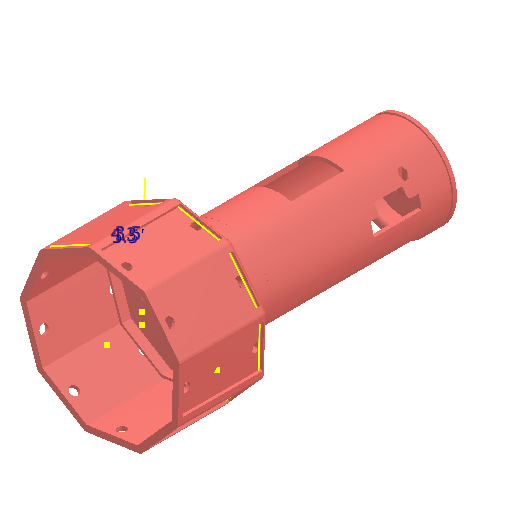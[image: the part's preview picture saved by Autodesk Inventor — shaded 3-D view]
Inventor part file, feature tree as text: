
AUTODESK INVENTOR PART (.ipt)
format: ipt  version: 2025 (Build 290162000, 162)  size: 1,940,480 bytes
history: native  units: in
note: dims shown in document units (in); Inventor stores cm internally (conversion verified against a paired STEP export)
features: sketch x63, extrude x58, fillet x11, plane x6, other x3, direct_edit x2, pattern_circular x2, move_body x2, reference x2, emboss x1, split x1, projected_geometry x1
ambient origin geometry x8: Origin, YZ Plane, XZ Plane, XY Plane, X Axis, Y Axis, Z Axis, Center Point
bodies: Solid1 (feature_tree), Body4 (feature_tree), Solid2 (feature_tree), Solid3 (feature_tree)
feature tree (152):
  direct_edit  "Direct Edit1"
  extrude  "Extrusion1"  Depth=0.2062in TaperAngle=0.0deg
  extrude  "Extrusion2"  Depth=0.1437in TaperAngle=0.0deg
  sketch  "Sketch3"  dims[d8=0.0787in d9=1.811in d10=0.0in]
  extrude  "Extrusion3"  Depth=1.811in TaperAngle=0.0deg
  sketch  "Sketch6"  dims[d13=0.0591in d14=0.0in d15=0.1969in]
  extrude  "Extrusion4"  Depth=0.9449in
  extrude  "Extrusion5"  Depth=0.1969in
  pattern_circular  "Circular Pattern1"  Count=9  [1 undecoded]
  extrude  "Extrusion6"  Depth=0.315in
  extrude  "Extrusion7"  Depth=1.4409in TaperAngle=0.0deg
  pattern_circular  "Circular Pattern2"  Count=9  [1 undecoded]
  fillet  "Fillet1"  Radius=0.1412in
  extrude  "Extrusion8"  Depth=0.063in
  extrude  "Extrusion9"  Depth=0.8312in TaperAngle=0.0deg
  extrude  "Extrusion10"  Depth=0.0787in
  extrude  "Extrusion11"  Depth=0.1688in TaperAngle=0.0deg
  direct_edit  "Direct Edit2"
  extrude  "Extrusion12"  Depth=1.1063in TaperAngle=0.0deg
  extrude  "Extrusion13"  Depth=0.4724in TaperAngle=0.0deg
  extrude  "Extrusion14"  Depth=1.8898in
  extrude  "Extrusion15"  Depth=1.2795in
  extrude  "Extrusion16"  Depth=0.0787in TaperAngle=0.0deg
  extrude  "Extrusion17"  Depth=0.0787in
  fillet  "Fillet2"  Radius=0.0787in
  fillet  "Fillet3"  Radius=0.0787in
  fillet  "Fillet4"  Radius=0.7338in
  fillet  "Fillet5"  Radius=0.3937in
  extrude  "Extrusion18"  Depth=0.8312in TaperAngle=0.0deg
  extrude  "Extrusion19"  Depth=0.1575in TaperAngle=0.0deg
  extrude  "Extrusion20"  Depth=0.1969in TaperAngle=0.0deg
  fillet  "Fillet6"  Radius=0.1781in
  sketch  "Sketch24"  dims[d78=1.3912in d79=0.1969in d80=0.0in d81=0.1781in d82=0.0in]
  extrude  "Extrusion22"  Depth=1.5438in TaperAngle=0.0deg
  fillet  "Fillet8"  Radius=2.7938in
  extrude  "Extrusion23"  Depth=0.2362in
  extrude  "Extrusion24"  Depth=1.7313in TaperAngle=0.0deg
  extrude  "Extrusion25"  Depth=0.1575in
  sketch  "Sketch30"  dims[d98=0.1575in d99=1.6334in d100=0.0in]
  sketch  "Sketch32"  dims[d101=3.5084in d102=0.0in d103=0.9459in d104=0.6917in d105=0.0in d106=0.0in]
  extrude  "Extrusion26"  Depth=1.6334in TaperAngle=0.0deg
  extrude  "Extrusion27"  Depth=0.9459in TaperAngle=0.0deg
  plane  "Work Plane3"
  extrude  "Extrusion28"  Depth=0.0787in TaperAngle=0.0deg
  sketch  "Sketch37"  dims[d118=0.0in d119=0.0in d120=0.0in d121=-0.3937in]
  extrude  "Extrusion29"  Depth=0.9375in
  extrude  "Extrusion30"  Depth=1.3563in TaperAngle=0.0deg
  extrude  "Extrusion31"  TaperAngle=0.0deg  [1 undecoded]
  extrude  "Extrusion32"  Depth=1.4562in TaperAngle=0.0deg
  sketch  "Sketch42"  dims[d136=4.9173in d137=0.0in d138=2.6535in d139=0.0in]
  extrude  "Extrusion33"  Depth=4.4562in TaperAngle=0.0deg
  sketch  "Sketch44"  dims[d144=0.6063in d145=0.0in d146=0.1378in]
  sketch  "Sketch45"  dims[d147=3.4188in d148=0.0in d149=0.2687in d150=0.0in]
  extrude  "Extrusion34"  Depth=0.9173in TaperAngle=0.0deg
  extrude  "Extrusion35"  Depth=2.6535in TaperAngle=0.0deg
  plane  "Work Plane6"
  plane  "Work Plane7"
  extrude  "Extrusion36"  Depth=4.4562in TaperAngle=0.0deg
  sketch  "Sketch49"  dims[d163=0.2062in d164=0.0in d165=0.2062in d166=0.0in]
  plane  "Work Plane8"
  emboss  "Emboss1"
  extrude  "Extrusion37"  Depth=0.1378in
  plane  "Work Plane9"
  split  "Split1"
  move_body  "Move Body1"
  extrude  "Extrusion38"  Depth=0.2687in TaperAngle=0.0deg
  extrude  "Extrusion39"  Depth=3.5438in TaperAngle=0.0deg
  sketch  "Sketch54"  dims[d178=0.0in d179=0.0in]
  extrude  "Extrusion40"  Depth=0.0812in TaperAngle=0.0deg
  extrude  "Extrusion41"  Depth=0.2953in TaperAngle=0.0deg
  extrude  "Extrusion42"  Depth=0.2062in TaperAngle=0.0deg
  extrude  "Extrusion43"  Depth=0.0787in
  extrude  "Extrusion44"  Depth=0.1388in TaperAngle=0.0deg
  extrude  "Extrusion45"  Depth=0.1388in TaperAngle=0.0deg
  extrude  "Extrusion46"  Depth=0.0394in
  extrude  "Extrusion47"  TaperAngle=0.0deg  [1 undecoded]
  sketch  "Sketch56"
  extrude  "Extrusion48"  [1 undecoded]
  extrude  "Extrusion49"  [1 undecoded]
  extrude  "Extrusion50"  [1 undecoded]
  extrude  "Extrusion51"  [1 undecoded]
  extrude  "Extrusion52"  [1 undecoded]
  extrude  "Extrusion53"  [1 undecoded]
  extrude  "Extrusion54"  [1 undecoded]
  extrude  "Extrusion55"  [1 undecoded]
  extrude  "Extrusion56"  [1 undecoded]
  fillet  "Fillet13"  [1 undecoded]
  fillet  "Fillet14"  [1 undecoded]
  extrude  "Extrusion57"  [1 undecoded]
  extrude  "Extrusion58"  [1 undecoded]
  sketch  "Sketch67"
  sketch  "Sketch68"
  extrude  "Extrusion59"  [1 undecoded]
  fillet  "Fillet15"  [1 undecoded]
  fillet  "Fillet16"  [1 undecoded]
  sketch  "Sketch1"  dims[d0=0.0in d1=0.0in d2=-0.6875in d3=0.2062in d4=0.0in]
  sketch  "Sketch2"  dims[d5=1.1811in d6=0.1437in d7=0.0in]
  sketch  "Sketch5"  dims[d11=1.7323in d12=0.9449in]
  sketch  "Sketch7"  dims[d16=0.1969in]
  sketch  "Sketch8"  dims[d17=0.1841in d18=0.0in d19=3.5433in d20=2.4737in]
  sketch  "Sketch9"  dims[d22=0.0787in d23=0.315in]
  sketch  "Sketch10"  dims[d24=0.0787in d25=1.4409in d26=0.0in]
  sketch  "Sketch11"  dims[d27=1.9966in d28=0.0in d29=3.5433in d30=2.4737in d32=0.1412in]
  sketch  "Sketch12"  dims[d33=0.063in d34=0.063in]
  sketch  "Sketch13"  dims[d35=0.2756in d36=0.0in d37=0.8312in d38=0.0in]
  sketch  "Sketch14"  dims[d39=1.1063in d40=0.0in d41=0.0787in]
  sketch  "Sketch15"  dims[d42=0.0787in d43=0.1688in d44=0.0in]
  sketch  "Sketch16"  dims[d45=0.5187in d46=0.0in d47=1.1063in d48=0.0in]
  sketch  "Sketch17"  dims[d49=1.6535in d50=0.4724in d51=0.0in]
  sketch  "Sketch18"  dims[d52=0.0787in d53=0.0in d54=1.8898in]
  sketch  "Sketch19"  dims[d55=0.2963in d56=0.0in d57=1.2795in]
  sketch  "Sketch20"  dims[d58=1.3583in d59=0.0787in d60=0.0in]
  sketch  "Sketch21"  dims[d61=0.0787in d62=0.0787in d63=0.0787in d64=0.0787in d65=0.7338in d66=0.0in d67=0.3937in d68=0.0in]
  sketch  "Sketch22"  dims[d69=0.0787in d70=0.8312in d71=0.0in]
  sketch  "Sketch23"  dims[d72=0.0787in d76=0.1575in d77=0.0in]
  sketch  "Sketch26"  dims[d83=0.1575in d84=0.0in d85=1.5438in d86=0.0in d87=2.7938in d88=0.0in]
  sketch  "Sketch27"  dims[d89=1.7313in d90=0.0in d91=0.2362in]
  sketch  "Sketch28"  dims[d92=0.2362in d93=1.7313in d94=0.0in]
  sketch  "Sketch29"  dims[d95=0.0709in d96=0.0in d97=0.1575in]
  sketch  "Sketch33"  dims[d107=0.1137in d108=0.0in d109=0.0787in d110=0.0in]
  sketch  "Sketch34"  dims[d111=1.6688in d112=0.0in d113=0.9375in]
  sketch  "Sketch36"  dims[d114=0.0394in d115=0.0in d116=1.3563in d117=0.0in]
  reference  "Reference1"
  reference  "Reference2"
  sketch  "Sketch39"  dims[d122=0.3937in d123=0.0in d124=1.4562in d125=0.0in]
  sketch  "Sketch40"  dims[d130=0.1693in d131=4.4562in d132=0.0in]
  sketch  "Sketch41"  dims[d133=0.2165in d134=0.9173in d135=0.0in]
  sketch  "Sketch43"  dims[d140=0.9247in d141=0.0in d142=4.4562in d143=0.0in]
  sketch  "Sketch46"  dims[d151=0.4813in d152=0.0in d153=3.5438in d154=0.0in]
  sketch  "Sketch47"  dims[d155=0.3937in d156=0.0in d157=0.0812in d158=0.0in]
  plane  "Work Plane5"
  sketch  "Sketch48"  dims[d159=0.2953in d160=0.0in d161=0.2953in d162=0.0in]
  sketch  "Sketch50"  dims[d167=0.0787in d168=0.0787in]
  sketch  "Sketch51"  dims[d169=1.7313in d170=0.0in d171=0.1388in d172=0.0in]
  sketch  "Sketch52"  dims[d173=1.9291in d174=0.1388in d175=0.0in]
  sketch  "Sketch53"  dims[d176=0.0945in d177=0.0394in]
  sketch  "Sketch55"
  sketch  "Sketch57"
  sketch  "Sketch58"
  sketch  "Sketch59"
  sketch  "Sketch60"
  sketch  "Sketch61"
  sketch  "Sketch62"
  sketch  "Sketch63"
  sketch  "Sketch64"
  sketch  "Sketch65"
  sketch  "Sketch66"
  move_body  "Move1"
  projected_geometry  "Project Cut Edges1"
  other  "Delete1"
  other  "Full assembly 2.iam"
  other  "main_board:1"
note: 20 required parameter values undecoded (feature->parameter linkage not recoverable at this tier; creation-order binding heuristic only, values carry confidence <= 0.55)
